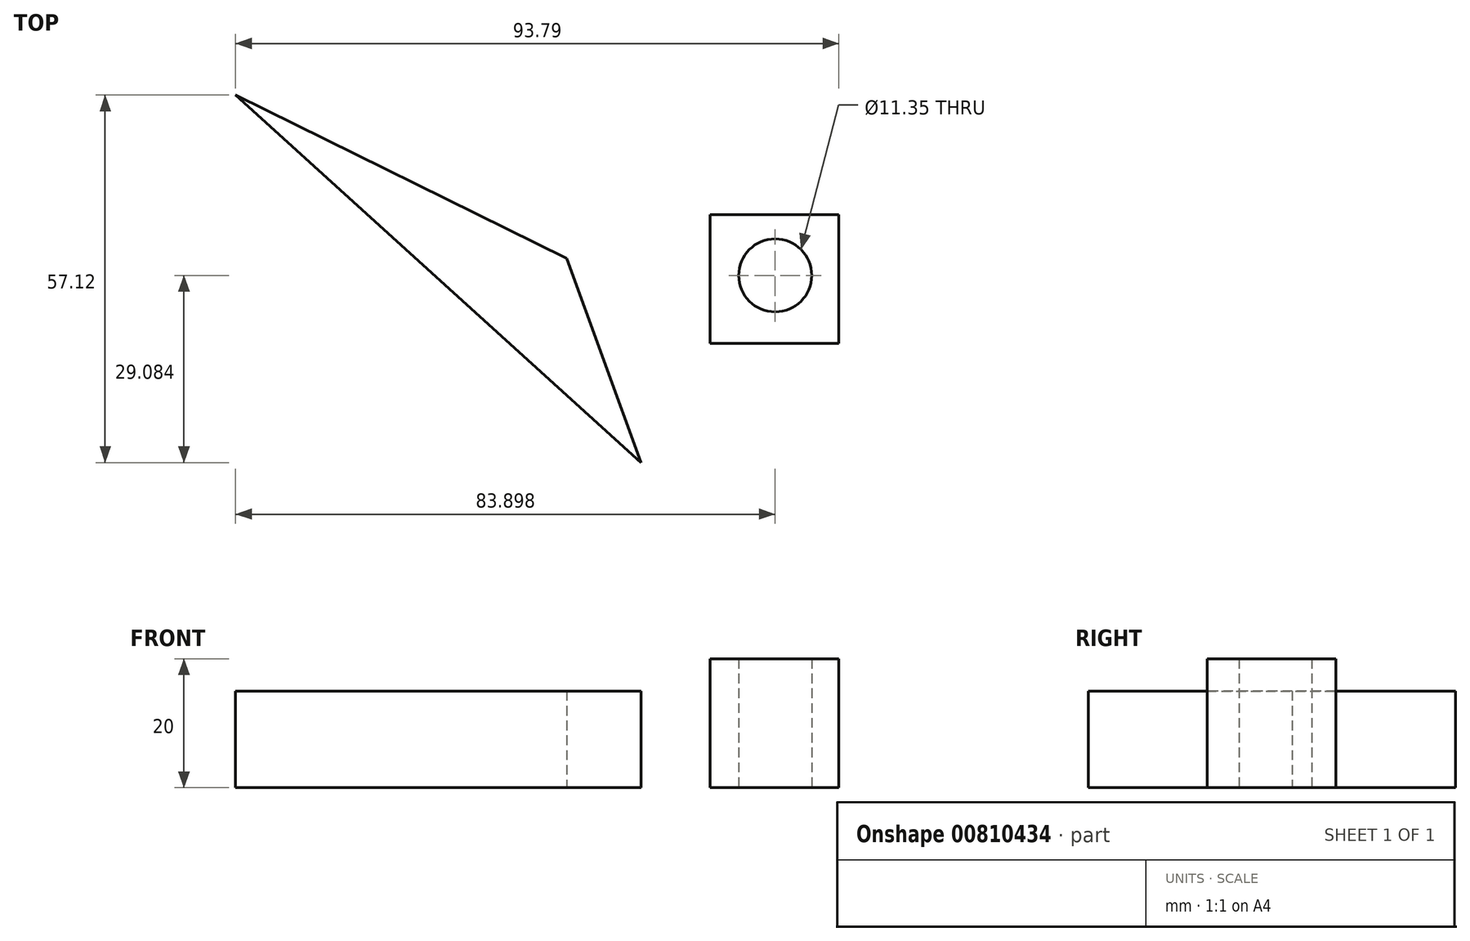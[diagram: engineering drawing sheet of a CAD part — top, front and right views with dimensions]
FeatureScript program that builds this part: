
annotation { "Feature Type Name" : "Feature", "Feature Type Description" : "" }
export const myFeature = defineFeature(function(context is Context, id is Id, definition is map)
    precondition{}
    {
        {
            var Q0;
            Q0=qCreatedBy(makeId("Top.planeOp"),FACE);
            var sketch = newSketch(context, id + "F0", { "sketchPlane" : qUnion([Q0])});
            skLineSegment(sketch, "E0", {"start": v(0, 0) * mm, "end": v(-63.07, 57.12) * mm});
            skLineSegment(sketch, "E1", {"start": v(-63.07, 57.12) * mm, "end": v(-11.56, 31.7) * mm});
            skLineSegment(sketch, "E2", {"start": v(-11.56, 31.7) * mm, "end": v(0, 0) * mm});
            skSolve(sketch);
        }
        {
            var Q0;
            Q0=makeQuery(id+"F0.imprint","IMPRINT",FACE,{"disambiguationData":[TD([[makeQuery(id+"F0.imprint","IMPRINT",EDGE,{"derivedFrom":sQuery(id+"F0.wireOp",EDGE,"E0")}),-1.0]])]});
            extrude(context, id + "F1", {"entities" : qUnion([Q0]), "depth" : 15 * mm, "offsetDistance" : 25 * mm});
        }
        {
            var Q0;
            Q0=qCreatedBy(makeId("Top.planeOp"),FACE);
            var sketch = newSketch(context, id + "F2", { "sketchPlane" : qUnion([Q0])});
            skLineSegment(sketch, "E3.bottom", {"start": v(10.72, 38.5) * mm, "end": v(30.72, 38.5) * mm});
            skLineSegment(sketch, "E3.top", {"start": v(10.72, 18.5) * mm, "end": v(30.72, 18.5) * mm});
            skLineSegment(sketch, "E3.left", {"start": v(10.72, 38.5) * mm, "end": v(10.72, 18.5) * mm});
            skLineSegment(sketch, "E3.right", {"start": v(30.72, 38.5) * mm, "end": v(30.72, 18.5) * mm});
            skSolve(sketch);
        }
        {
            var Q0;
            Q0=makeQuery(id+"F2.imprint","IMPRINT",FACE,{"disambiguationData":[TD([[makeQuery(id+"F2.imprint","IMPRINT",EDGE,{"derivedFrom":sQuery(id+"F2.wireOp",EDGE,"E3.bottom")}),-1.0]])]});
            extrude(context, id + "F3", {"entities" : qUnion([Q0]), "depth" : 20 * mm, "offsetDistance" : 25 * mm});
        }
        {
            var Q0;
            Q0 = qSketchRegion(id + "F2", true);
            extrude(context, id + "F4", {"entities" : qUnion([Q0]), "operationType" : NewBodyOperationType.ADD, "depth" : 20 * mm, "offsetDistance" : 25 * mm});
        }
        {
            var Q0;
            Q0=qCreatedBy(makeId("Top.planeOp"),FACE);
            var sketch = newSketch(context, id + "F5", { "sketchPlane" : qUnion([Q0])});
            skCircle(sketch, "E4", {"center": v(20.83, 29.08) * mm, "radius": 5.67 * mm});
            skSolve(sketch);
        }
        {
            var Q0;
            Q0 = qSketchRegion(id + "F5", true);
            extrude(context, id + "F6", {"entities" : qUnion([Q0]), "operationType" : NewBodyOperationType.REMOVE, "oppositeDirection" : true, "depth" : -20 * mm, "offsetDistance" : 25 * mm});
        }
    });
